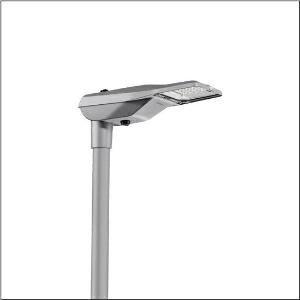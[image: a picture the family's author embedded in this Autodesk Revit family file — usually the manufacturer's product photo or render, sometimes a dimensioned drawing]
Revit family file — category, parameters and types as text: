
# Revit family: streetlight_sl_21_iq_micro___st1_5a_5xe1p31y08db_002f
name_source: partatom
category: Lighting Fixtures
units: mm (PartAtom-declared; Revit-internal decimal feet)

## family parameters
Cut with Voids When Loaded = No
Host = Face
Light Source = No
Part Type = Normal
Room Calculation Point = No
Round Connector Dimension = Use Diameter
Shared = No

## types (1)
- --- (1 x LED, 5030 lm, 39.1 W, 3000K)
    Apparent Load = 39 VA
    CIE Flux Codes = 22 53 95 100 100
    Color Rendering = 70
    Color Temperature = 3000K
    Default Elevation = 1800 mm
    Description = Streetlight SL 21 iQ micro, mast luminaire, primary light control with lens, of PMMA, primary optical cover: cover, of toughened safety glass, transparent, light distribution: ST1.5a, light emission: direct distribution, primary light characteristic: asymmetric, installation type: post-top, side-entry, LED, High Power LED, rated luminous flux: 5.030lm, luminous efficacy: 129lm/W, light colour: 730, colour temperature: 3000K, control gear: iQ-Street Remote, D4i with power reduction, control: pre-setting: logarithmic dimming characteristic, Street-Remote, Auto-Match, Temp-Guard, Lumen-Switch, Night-Set, Smart-Wire, Light-Fading, Desk-Remote (wireless, voltage-free reading and setting of iQ features in the workshop via application-optimized NFC function/RFID function), optimised constant luminous flux control (CLO 2.0), mains connection: 220..240V, AC, 50/60Hz, start of lifetime: 39W, end of service life: 41W, reduction: 17W, luminaire housing, of diecast aluminium, powder-coated, SITECO metallic grey (DB 702S), corrosivity category C5 high according to DIN EN ISO 12944, please order mast flange separately, inclination adjustable: 0°, 5°, 10°, 15°, sealing non-destructively replaceable, multi-level sealing system, length: 528mm, width: 235mm, height: 110mm, mast flange for spigot size: 42mm (side-entry): 5XC10008XM4, 60/48mm (side-entry/post-top): 5XC10108XM2, 76/60mm (side-entry/post-top): 5XC10108XM1, mounting height: 4..8m, Smart Interface below and above, protection rating (complete): IP66, insulation class (complete): insulation class II (safety insulation), certification: CE, ENEC, ENEC+, VDE, impact resistance: IK10, permissible operating ambient temperature for outdoor applications: -40..+50°C, standard-compliant lighting for roads and squares, packaging unit: 1 piece

Light Distribution: ST1.5a
    Height = 110 mm
    Lamp = 1 x LED
    Lamp Light Flux = 5030 lm
    Lamp Power = 39.1 W
    Lamp count = 1
    Length = 528 mm
    Luminous efficacy = 129 lm/W
    Manufacturer = Siteco
    ModVariant = No
    Model = 5XE1P31Y08DB
    Mounting Place = Pole
    Mounting Type = Pole top
    Number of Poles = 1
    OnlyDefault = Yes
    Power Factor = 1
    Product Name = Streetlight SL 21 iQ micro | ST1.5a
    Product group = mast luminaire | pylon top
    ProductGroupID = 6100
    Protection Class = Protection class II
    Protection Degree = IP 66
    RLX_Detail_Level = 1
    RLX_Emergency_Light_Flux = 0 lm
    RLX_Emergency_Type = 0
    RLX_Emergency_Type_DB = No
    RlxData = <blob elided: 102409 chars, md5=056ea5c4>
    Socket = socket
    Standby Power = 0 W
    System Light Flux = 5030 lm
    System Power = 39 W
    Type Comments = factory setting: luminous flux: 100 % | dim-lin: 254 | 765 mA
    Type Image = l_1007239.jpg
    URL = http://relux.com
    VarID = @adj_113485
    Voltage = 0 V
    Weight = 0.00 kg
    Width = 235 mm

## geometry (parser evidence)
native form markers: Blend x4, Sweep x9
no freeform markers — native parametric forms only
